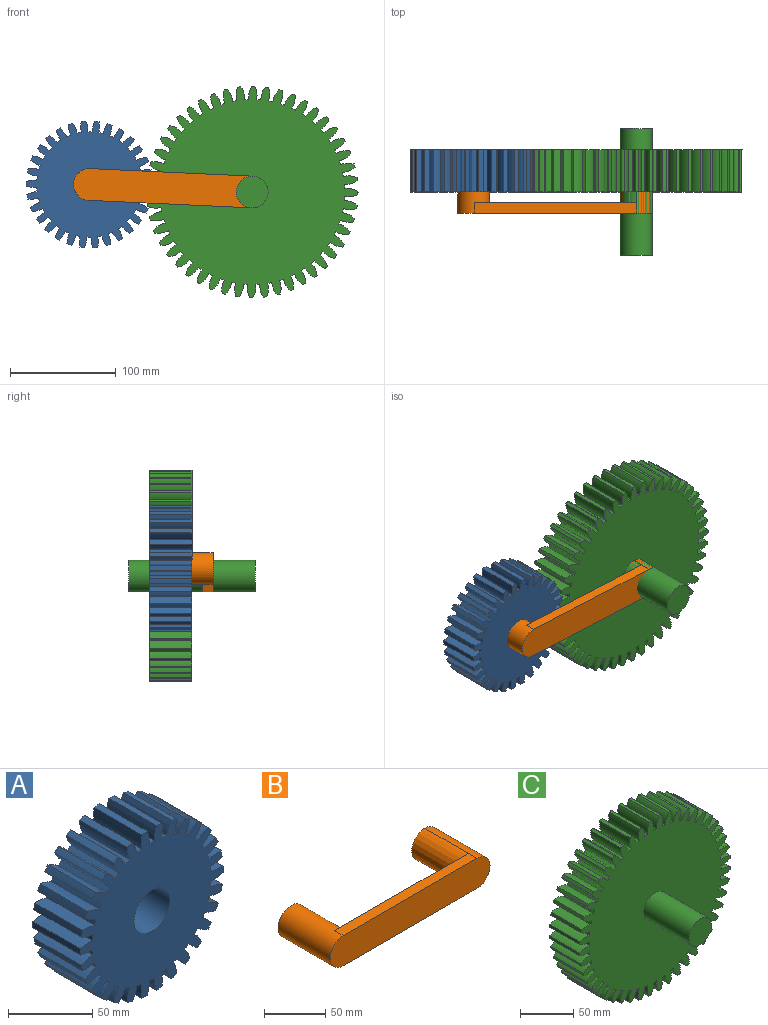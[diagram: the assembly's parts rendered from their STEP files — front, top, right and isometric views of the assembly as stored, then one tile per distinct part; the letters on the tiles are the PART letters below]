
ASSEMBLY  parts=3 mates=2
PART A: 123 faces, bbox 120x40x119.7 mm
  f0: cylinder r=60mm len=40mm, axis (0,1,0), area 182.4mm2, adj f1,f118,f120,f121
  f1: cylinder r=28.31mm len=40mm, axis (0,1,0), area 406.4mm2, adj f0,f3,f120,f121
  f2: cylinder r=28.31mm len=40mm, axis (0,1,0), area 406.4mm2, adj f3,f4,f120,f121
  f3: cylinder r=50mm len=40mm, axis (0,1,0), area 160mm2, adj f1,f2,f120,f121
  f4: cylinder r=60mm len=40mm, axis (0,1,0), area 182.4mm2, adj f2,f5,f120,f121
  f5: cylinder r=28.31mm len=40mm, axis (0,1,0), area 406.4mm2, adj f4,f7,f120,f121
  f6: cylinder r=28.31mm len=40mm, axis (0,1,0), area 406.4mm2, adj f7,f8,f120,f121
  f7: cylinder r=50mm len=40mm, axis (0,1,0), area 160mm2, adj f5,f6,f120,f121
  f8: cylinder r=60mm len=40mm, axis (0,1,0), area 182.4mm2, adj f6,f9,f120,f121
  f9: cylinder r=28.31mm len=40mm, axis (0,1,0), area 406.4mm2, adj f8,f11,f120,f121
  f10: cylinder r=28.31mm len=40mm, axis (0,1,0), area 406.4mm2, adj f11,f12,f120,f121
  f11: cylinder r=50mm len=40mm, axis (0,1,0), area 160mm2, adj f9,f10,f120,f121
  f12: cylinder r=60mm len=40mm, axis (0,1,0), area 182.4mm2, adj f10,f13,f120,f121
  f13: cylinder r=28.31mm len=40mm, axis (0,1,0), area 406.4mm2, adj f12,f15,f120,f121
  f14: cylinder r=28.31mm len=40mm, axis (0,1,0), area 406.4mm2, adj f15,f16,f120,f121
  f15: cylinder r=50mm len=40mm, axis (0,1,0), area 160mm2, adj f13,f14,f120,f121
  f16: cylinder r=60mm len=40mm, axis (0,1,0), area 182.4mm2, adj f14,f17,f120,f121
  f17: cylinder r=28.31mm len=40mm, axis (0,1,0), area 406.4mm2, adj f16,f19,f120,f121
  f18: cylinder r=28.31mm len=40mm, axis (0,1,0), area 406.4mm2, adj f19,f20,f120,f121
  f19: cylinder r=50mm len=40mm, axis (0,1,0), area 160mm2, adj f17,f18,f120,f121
  f20: cylinder r=60mm len=40mm, axis (0,1,0), area 182.4mm2, adj f18,f21,f120,f121
  f21: cylinder r=28.31mm len=40mm, axis (0,1,0), area 406.4mm2, adj f20,f23,f120,f121
  f22: cylinder r=28.31mm len=40mm, axis (0,1,0), area 406.4mm2, adj f23,f24,f120,f121
  f23: cylinder r=50mm len=40mm, axis (0,1,0), area 160mm2, adj f21,f22,f120,f121
  f24: cylinder r=60mm len=40mm, axis (0,1,0), area 182.4mm2, adj f22,f25,f120,f121
  f25: cylinder r=28.31mm len=40mm, axis (0,1,0), area 406.4mm2, adj f24,f27,f120,f121
  f26: cylinder r=28.31mm len=40mm, axis (0,1,0), area 406.4mm2, adj f27,f28,f120,f121
  f27: cylinder r=50mm len=40mm, axis (0,1,0), area 160mm2, adj f25,f26,f120,f121
  f28: cylinder r=60mm len=40mm, axis (0,1,0), area 182.4mm2, adj f26,f29,f120,f121
  f29: cylinder r=28.31mm len=40mm, axis (0,1,0), area 406.4mm2, adj f28,f31,f120,f121
  f30: cylinder r=28.31mm len=40mm, axis (0,1,0), area 406.4mm2, adj f31,f32,f120,f121
  f31: cylinder r=50mm len=40mm, axis (0,1,0), area 160mm2, adj f29,f30,f120,f121
  f32: cylinder r=60mm len=40mm, axis (0,1,0), area 182.4mm2, adj f30,f33,f120,f121
  f33: cylinder r=28.31mm len=40mm, axis (0,1,0), area 406.4mm2, adj f32,f35,f120,f121
  f34: cylinder r=28.31mm len=40mm, axis (0,1,0), area 406.4mm2, adj f35,f36,f120,f121
  f35: cylinder r=50mm len=40mm, axis (0,1,0), area 160mm2, adj f33,f34,f120,f121
  f36: cylinder r=60mm len=40mm, axis (0,1,0), area 182.4mm2, adj f34,f37,f120,f121
  f37: cylinder r=28.31mm len=40mm, axis (0,1,0), area 406.4mm2, adj f36,f39,f120,f121
  f38: cylinder r=28.31mm len=40mm, axis (0,1,0), area 406.4mm2, adj f39,f40,f120,f121
  f39: cylinder r=50mm len=40mm, axis (0,1,0), area 160mm2, adj f37,f38,f120,f121
  f40: cylinder r=60mm len=40mm, axis (0,1,0), area 182.4mm2, adj f38,f41,f120,f121
  f41: cylinder r=28.31mm len=40mm, axis (0,1,0), area 406.4mm2, adj f40,f43,f120,f121
  f42: cylinder r=28.31mm len=40mm, axis (0,1,0), area 406.4mm2, adj f43,f44,f120,f121
  f43: cylinder r=50mm len=40mm, axis (0,1,0), area 160mm2, adj f41,f42,f120,f121
  f44: cylinder r=60mm len=40mm, axis (0,1,0), area 182.4mm2, adj f42,f45,f120,f121
  f45: cylinder r=28.31mm len=40mm, axis (0,1,0), area 406.4mm2, adj f44,f47,f120,f121
  f46: cylinder r=28.31mm len=40mm, axis (0,1,0), area 406.4mm2, adj f47,f48,f120,f121
  f47: cylinder r=50mm len=40mm, axis (0,1,0), area 160mm2, adj f45,f46,f120,f121
  f48: cylinder r=60mm len=40mm, axis (0,1,0), area 182.4mm2, adj f46,f49,f120,f121
  f49: cylinder r=28.31mm len=40mm, axis (0,1,0), area 406.4mm2, adj f48,f51,f120,f121
  f50: cylinder r=28.31mm len=40mm, axis (0,1,0), area 406.4mm2, adj f51,f52,f120,f121
  f51: cylinder r=50mm len=40mm, axis (0,1,0), area 160mm2, adj f49,f50,f120,f121
  f52: cylinder r=60mm len=40mm, axis (0,1,0), area 182.4mm2, adj f50,f53,f120,f121
  f53: cylinder r=28.31mm len=40mm, axis (0,1,0), area 406.4mm2, adj f52,f55,f120,f121
  f54: cylinder r=28.31mm len=40mm, axis (0,1,0), area 406.4mm2, adj f55,f56,f120,f121
  f55: cylinder r=50mm len=40mm, axis (0,1,0), area 160mm2, adj f53,f54,f120,f121
  f56: cylinder r=60mm len=40mm, axis (0,1,0), area 182.4mm2, adj f54,f57,f120,f121
  f57: cylinder r=28.31mm len=40mm, axis (0,1,0), area 406.4mm2, adj f56,f59,f120,f121
  f58: cylinder r=28.31mm len=40mm, axis (0,1,0), area 406.4mm2, adj f59,f60,f120,f121
  f59: cylinder r=50mm len=40mm, axis (0,1,0), area 160mm2, adj f57,f58,f120,f121
  f60: cylinder r=60mm len=40mm, axis (0,1,0), area 182.4mm2, adj f58,f61,f120,f121
  f61: cylinder r=28.31mm len=40mm, axis (0,1,0), area 406.4mm2, adj f60,f63,f120,f121
  f62: cylinder r=28.31mm len=40mm, axis (0,1,0), area 406.4mm2, adj f63,f64,f120,f121
  f63: cylinder r=50mm len=40mm, axis (0,1,0), area 160mm2, adj f61,f62,f120,f121
  f64: cylinder r=60mm len=40mm, axis (0,1,0), area 182.4mm2, adj f62,f65,f120,f121
  f65: cylinder r=28.31mm len=40mm, axis (0,1,0), area 406.4mm2, adj f64,f67,f120,f121
  f66: cylinder r=28.31mm len=40mm, axis (0,1,0), area 406.4mm2, adj f67,f68,f120,f121
  f67: cylinder r=50mm len=40mm, axis (0,1,0), area 160mm2, adj f65,f66,f120,f121
  f68: cylinder r=60mm len=40mm, axis (0,1,0), area 182.4mm2, adj f66,f69,f120,f121
  f69: cylinder r=28.31mm len=40mm, axis (0,1,0), area 406.4mm2, adj f68,f71,f120,f121
  f70: cylinder r=28.31mm len=40mm, axis (0,1,0), area 406.4mm2, adj f71,f72,f120,f121
  f71: cylinder r=50mm len=40mm, axis (0,1,0), area 160mm2, adj f69,f70,f120,f121
  f72: cylinder r=60mm len=40mm, axis (0,1,0), area 182.4mm2, adj f70,f73,f120,f121
  f73: cylinder r=28.31mm len=40mm, axis (0,1,0), area 406.4mm2, adj f72,f75,f120,f121
  f74: cylinder r=28.31mm len=40mm, axis (0,1,0), area 406.4mm2, adj f75,f76,f120,f121
  f75: cylinder r=50mm len=40mm, axis (0,1,0), area 160mm2, adj f73,f74,f120,f121
  f76: cylinder r=60mm len=40mm, axis (0,1,0), area 182.4mm2, adj f74,f77,f120,f121
  f77: cylinder r=28.31mm len=40mm, axis (0,1,0), area 406.4mm2, adj f76,f79,f120,f121
  f78: cylinder r=28.31mm len=40mm, axis (0,1,0), area 406.4mm2, adj f79,f80,f120,f121
  f79: cylinder r=50mm len=40mm, axis (0,1,0), area 160mm2, adj f77,f78,f120,f121
  f80: cylinder r=60mm len=40mm, axis (0,1,0), area 182.4mm2, adj f78,f81,f120,f121
  f81: cylinder r=28.31mm len=40mm, axis (0,1,0), area 406.4mm2, adj f80,f83,f120,f121
  f82: cylinder r=28.31mm len=40mm, axis (0,1,0), area 406.4mm2, adj f83,f84,f120,f121
  f83: cylinder r=50mm len=40mm, axis (0,1,0), area 160mm2, adj f81,f82,f120,f121
  f84: cylinder r=60mm len=40mm, axis (0,1,0), area 182.4mm2, adj f82,f85,f120,f121
  f85: cylinder r=28.31mm len=40mm, axis (0,1,0), area 406.4mm2, adj f84,f87,f120,f121
  f86: cylinder r=28.31mm len=40mm, axis (0,1,0), area 406.4mm2, adj f87,f88,f120,f121
  f87: cylinder r=50mm len=40mm, axis (0,1,0), area 160mm2, adj f85,f86,f120,f121
  f88: cylinder r=60mm len=40mm, axis (0,1,0), area 182.4mm2, adj f86,f89,f120,f121
  f89: cylinder r=28.31mm len=40mm, axis (0,1,0), area 406.4mm2, adj f88,f91,f120,f121
  f90: cylinder r=28.31mm len=40mm, axis (0,1,0), area 406.4mm2, adj f91,f92,f120,f121
  f91: cylinder r=50mm len=40mm, axis (0,1,0), area 160mm2, adj f89,f90,f120,f121
  f92: cylinder r=60mm len=40mm, axis (0,1,0), area 182.4mm2, adj f90,f93,f120,f121
  f93: cylinder r=28.31mm len=40mm, axis (0,1,0), area 406.4mm2, adj f92,f95,f120,f121
  f94: cylinder r=28.31mm len=40mm, axis (0,1,0), area 406.4mm2, adj f95,f96,f120,f121
  f95: cylinder r=50mm len=40mm, axis (0,1,0), area 160mm2, adj f93,f94,f120,f121
  f96: cylinder r=60mm len=40mm, axis (0,1,0), area 182.4mm2, adj f94,f97,f120,f121
  f97: cylinder r=28.31mm len=40mm, axis (0,1,0), area 406.4mm2, adj f96,f99,f120,f121
  f98: cylinder r=28.31mm len=40mm, axis (0,1,0), area 406.4mm2, adj f99,f100,f120,f121
  f99: cylinder r=50mm len=40mm, axis (0,1,0), area 160mm2, adj f97,f98,f120,f121
  f100: cylinder r=60mm len=40mm, axis (0,1,0), area 182.4mm2, adj f98,f101,f120,f121
  f101: cylinder r=28.31mm len=40mm, axis (0,1,0), area 406.4mm2, adj f100,f103,f120,f121
  f102: cylinder r=28.31mm len=40mm, axis (0,1,0), area 406.4mm2, adj f103,f104,f120,f121
  f103: cylinder r=50mm len=40mm, axis (0,1,0), area 160mm2, adj f101,f102,f120,f121
  f104: cylinder r=60mm len=40mm, axis (0,1,0), area 182.4mm2, adj f102,f105,f120,f121
  f105: cylinder r=28.31mm len=40mm, axis (0,1,0), area 406.4mm2, adj f104,f107,f120,f121
  f106: cylinder r=28.31mm len=40mm, axis (0,1,0), area 406.4mm2, adj f107,f108,f120,f121
  f107: cylinder r=50mm len=40mm, axis (0,1,0), area 160mm2, adj f105,f106,f120,f121
  f108: cylinder r=60mm len=40mm, axis (0,1,0), area 182.4mm2, adj f106,f109,f120,f121
  f109: cylinder r=28.31mm len=40mm, axis (0,1,0), area 406.4mm2, adj f108,f111,f120,f121
  f110: cylinder r=28.31mm len=40mm, axis (0,1,0), area 406.4mm2, adj f111,f112,f120,f121
  f111: cylinder r=50mm len=40mm, axis (0,1,0), area 160mm2, adj f109,f110,f120,f121
  f112: cylinder r=60mm len=40mm, axis (0,1,0), area 182.4mm2, adj f110,f113,f120,f121
  f113: cylinder r=28.31mm len=40mm, axis (0,1,0), area 406.4mm2, adj f112,f115,f120,f121
  f114: cylinder r=28.31mm len=40mm, axis (0,1,0), area 406.4mm2, adj f115,f117,f120,f121
  f115: cylinder r=50mm len=40mm, axis (0,1,0), area 160mm2, adj f113,f114,f120,f121
  f116: cylinder r=28.31mm len=40mm, axis (0,1,0), area 406.4mm2, adj f117,f119,f120,f121
  f117: cylinder r=60mm len=40mm, axis (0,1,0), area 182.4mm2, adj f114,f116,f120,f121
  f118: cylinder r=28.31mm len=40mm, axis (0,1,0), area 406.4mm2, adj f0,f119,f120,f121
  f119: cylinder r=50mm len=40mm, axis (0,1,0), area 160mm2, adj f116,f118,f120,f121
  f120: plane 120x119.73mm, normal (0,-1,0), area 8985.6mm2, adj f0,f1,f2,f3,f4,f5,f6,f7
  f121: plane 120x119.73mm, normal (0,1,0), area 8985.6mm2, adj f0,f1,f2,f3,f4,f5,f6,f7
  f122: cylinder r=15mm len=40mm, axis (0,-1,0), area 3769.9mm2, adj f120,f121
PART B: 9 faces, bbox 184x60x30 mm
  f0: cylinder r=15mm len=60mm, axis (0,1,0), area 5183.6mm2, adj f1,f2,f3,f4,f5
  f1: plane 184x30mm, normal (0,-1,0), area 5326.9mm2, adj f0,f4,f5,f6
  f2: plane 30x30mm, normal (0,1,0), area 706.9mm2, adj f0
  f3: plane 154x30mm, normal (0,1,0), area 3913.2mm2, adj f0,f4,f5,f7
  f4: plane 154x10mm, normal (0,0,1), area 1540mm2, adj f0,f1,f3,f6
  f5: plane 154x10mm, normal (0,0,-1), area 1540mm2, adj f0,f1,f3,f6
  f6: cylinder r=15mm len=60mm, axis (0,-1,0), area 2827.4mm2, adj f1,f4,f5,f7,f8
  f7: extruded ~50x30mm, area 2356.6mm2, adj f3,f6,f8
  f8: plane 30x30mm, normal (0,1,0), area 706.8mm2, adj f6,f7
PART C: 198 faces, bbox 199.8x120x199.8 mm
  f0: cylinder r=100mm len=40mm, axis (0,1,0), area 123.4mm2, adj f1,f188,f192,f193
  f1: cylinder r=19.38mm len=40mm, axis (0,1,0), area 517.2mm2, adj f0,f3,f192,f193
  f2: cylinder r=19.56mm len=40mm, axis (0,1,0), area 522.9mm2, adj f3,f4,f192,f193
  f3: cylinder r=87.5mm len=40mm, axis (0,1,0), area 160mm2, adj f1,f2,f192,f193
  f4: cylinder r=100mm len=40mm, axis (0,1,0), area 123.4mm2, adj f2,f5,f192,f193
  f5: cylinder r=19.38mm len=40mm, axis (0,1,0), area 517.2mm2, adj f4,f7,f192,f193
  f6: cylinder r=19.56mm len=40mm, axis (0,1,0), area 522.9mm2, adj f7,f8,f192,f193
  f7: cylinder r=87.5mm len=40mm, axis (0,1,0), area 160mm2, adj f5,f6,f192,f193
  f8: cylinder r=100mm len=40mm, axis (0,1,0), area 123.4mm2, adj f6,f9,f192,f193
  f9: cylinder r=19.38mm len=40mm, axis (0,1,0), area 517.2mm2, adj f8,f11,f192,f193
  f10: cylinder r=19.56mm len=40mm, axis (0,1,0), area 522.9mm2, adj f11,f12,f192,f193
  f11: cylinder r=87.5mm len=40mm, axis (0,1,0), area 160mm2, adj f9,f10,f192,f193
  f12: cylinder r=100mm len=40mm, axis (0,1,0), area 123.4mm2, adj f10,f13,f192,f193
  f13: cylinder r=19.38mm len=40mm, axis (0,1,0), area 517.2mm2, adj f12,f15,f192,f193
  f14: cylinder r=19.56mm len=40mm, axis (0,1,0), area 522.9mm2, adj f15,f16,f192,f193
  f15: cylinder r=87.5mm len=40mm, axis (0,1,0), area 160mm2, adj f13,f14,f192,f193
  f16: cylinder r=100mm len=40mm, axis (0,1,0), area 123.4mm2, adj f14,f17,f192,f193
  f17: cylinder r=19.38mm len=40mm, axis (0,1,0), area 517.2mm2, adj f16,f19,f192,f193
  f18: cylinder r=19.56mm len=40mm, axis (0,1,0), area 522.9mm2, adj f19,f20,f192,f193
  f19: cylinder r=87.5mm len=40mm, axis (0,1,0), area 160mm2, adj f17,f18,f192,f193
  f20: cylinder r=100mm len=40mm, axis (0,1,0), area 123.4mm2, adj f18,f21,f192,f193
  f21: cylinder r=19.38mm len=40mm, axis (0,1,0), area 517.2mm2, adj f20,f23,f192,f193
  f22: cylinder r=19.56mm len=40mm, axis (0,1,0), area 522.9mm2, adj f23,f24,f192,f193
  f23: cylinder r=87.5mm len=40mm, axis (0,1,0), area 160mm2, adj f21,f22,f192,f193
  f24: cylinder r=100mm len=40mm, axis (0,1,0), area 123.4mm2, adj f22,f25,f192,f193
  f25: cylinder r=19.38mm len=40mm, axis (0,1,0), area 517.2mm2, adj f24,f27,f192,f193
  f26: cylinder r=19.56mm len=40mm, axis (0,1,0), area 522.9mm2, adj f27,f28,f192,f193
  f27: cylinder r=87.5mm len=40mm, axis (0,1,0), area 160mm2, adj f25,f26,f192,f193
  f28: cylinder r=100mm len=40mm, axis (0,1,0), area 123.4mm2, adj f26,f29,f192,f193
  f29: cylinder r=19.38mm len=40mm, axis (0,1,0), area 517.2mm2, adj f28,f31,f192,f193
  f30: cylinder r=19.56mm len=40mm, axis (0,1,0), area 522.9mm2, adj f31,f32,f192,f193
  f31: cylinder r=87.5mm len=40mm, axis (0,1,0), area 160mm2, adj f29,f30,f192,f193
  f32: cylinder r=100mm len=40mm, axis (0,1,0), area 123.4mm2, adj f30,f33,f192,f193
  f33: cylinder r=19.38mm len=40mm, axis (0,1,0), area 517.2mm2, adj f32,f35,f192,f193
  f34: cylinder r=19.56mm len=40mm, axis (0,1,0), area 522.9mm2, adj f35,f36,f192,f193
  f35: cylinder r=87.5mm len=40mm, axis (0,1,0), area 160mm2, adj f33,f34,f192,f193
  f36: cylinder r=100mm len=40mm, axis (0,1,0), area 123.4mm2, adj f34,f37,f192,f193
  f37: cylinder r=19.38mm len=40mm, axis (0,1,0), area 517.2mm2, adj f36,f39,f192,f193
  f38: cylinder r=19.56mm len=40mm, axis (0,1,0), area 522.9mm2, adj f39,f40,f192,f193
  f39: cylinder r=87.5mm len=40mm, axis (0,1,0), area 160mm2, adj f37,f38,f192,f193
  f40: cylinder r=100mm len=40mm, axis (0,1,0), area 123.4mm2, adj f38,f41,f192,f193
  f41: cylinder r=19.38mm len=40mm, axis (0,1,0), area 517.2mm2, adj f40,f43,f192,f193
  f42: cylinder r=19.56mm len=40mm, axis (0,1,0), area 522.9mm2, adj f43,f44,f192,f193
  f43: cylinder r=87.5mm len=40mm, axis (0,1,0), area 160mm2, adj f41,f42,f192,f193
  f44: cylinder r=100mm len=40mm, axis (0,1,0), area 123.4mm2, adj f42,f45,f192,f193
  f45: cylinder r=19.38mm len=40mm, axis (0,1,0), area 517.2mm2, adj f44,f47,f192,f193
  f46: cylinder r=19.56mm len=40mm, axis (0,1,0), area 522.9mm2, adj f47,f48,f192,f193
  f47: cylinder r=87.5mm len=40mm, axis (0,1,0), area 160mm2, adj f45,f46,f192,f193
  f48: cylinder r=100mm len=40mm, axis (0,1,0), area 123.4mm2, adj f46,f49,f192,f193
  f49: cylinder r=19.38mm len=40mm, axis (0,1,0), area 517.2mm2, adj f48,f51,f192,f193
  f50: cylinder r=19.56mm len=40mm, axis (0,1,0), area 522.9mm2, adj f51,f52,f192,f193
  f51: cylinder r=87.5mm len=40mm, axis (0,1,0), area 160mm2, adj f49,f50,f192,f193
  f52: cylinder r=100mm len=40mm, axis (0,1,0), area 123.4mm2, adj f50,f53,f192,f193
  f53: cylinder r=19.38mm len=40mm, axis (0,1,0), area 517.2mm2, adj f52,f55,f192,f193
  f54: cylinder r=19.56mm len=40mm, axis (0,1,0), area 522.9mm2, adj f55,f56,f192,f193
  f55: cylinder r=87.5mm len=40mm, axis (0,1,0), area 160mm2, adj f53,f54,f192,f193
  f56: cylinder r=100mm len=40mm, axis (0,1,0), area 123.4mm2, adj f54,f57,f192,f193
  f57: cylinder r=19.38mm len=40mm, axis (0,1,0), area 517.2mm2, adj f56,f59,f192,f193
  f58: cylinder r=19.56mm len=40mm, axis (0,1,0), area 522.9mm2, adj f59,f60,f192,f193
  f59: cylinder r=87.5mm len=40mm, axis (0,1,0), area 160mm2, adj f57,f58,f192,f193
  f60: cylinder r=100mm len=40mm, axis (0,1,0), area 123.4mm2, adj f58,f61,f192,f193
  f61: cylinder r=19.38mm len=40mm, axis (0,1,0), area 517.2mm2, adj f60,f63,f192,f193
  f62: cylinder r=19.56mm len=40mm, axis (0,1,0), area 522.9mm2, adj f63,f64,f192,f193
  f63: cylinder r=87.5mm len=40mm, axis (0,1,0), area 160mm2, adj f61,f62,f192,f193
  f64: cylinder r=100mm len=40mm, axis (0,1,0), area 123.4mm2, adj f62,f65,f192,f193
  f65: cylinder r=19.38mm len=40mm, axis (0,1,0), area 517.2mm2, adj f64,f67,f192,f193
  f66: cylinder r=19.56mm len=40mm, axis (0,1,0), area 522.9mm2, adj f67,f68,f192,f193
  f67: cylinder r=87.5mm len=40mm, axis (0,1,0), area 160mm2, adj f65,f66,f192,f193
  f68: cylinder r=100mm len=40mm, axis (0,1,0), area 123.4mm2, adj f66,f69,f192,f193
  f69: cylinder r=19.38mm len=40mm, axis (0,1,0), area 517.2mm2, adj f68,f71,f192,f193
  f70: cylinder r=19.56mm len=40mm, axis (0,1,0), area 522.9mm2, adj f71,f72,f192,f193
  f71: cylinder r=87.5mm len=40mm, axis (0,1,0), area 160mm2, adj f69,f70,f192,f193
  f72: cylinder r=100mm len=40mm, axis (0,1,0), area 123.4mm2, adj f70,f73,f192,f193
  f73: cylinder r=19.38mm len=40mm, axis (0,1,0), area 517.2mm2, adj f72,f75,f192,f193
  f74: cylinder r=19.56mm len=40mm, axis (0,1,0), area 522.9mm2, adj f75,f76,f192,f193
  f75: cylinder r=87.5mm len=40mm, axis (0,1,0), area 160mm2, adj f73,f74,f192,f193
  f76: cylinder r=100mm len=40mm, axis (0,1,0), area 123.4mm2, adj f74,f77,f192,f193
  f77: cylinder r=19.38mm len=40mm, axis (0,1,0), area 517.2mm2, adj f76,f79,f192,f193
  f78: cylinder r=19.56mm len=40mm, axis (0,1,0), area 522.9mm2, adj f79,f80,f192,f193
  f79: cylinder r=87.5mm len=40mm, axis (0,1,0), area 160mm2, adj f77,f78,f192,f193
  f80: cylinder r=100mm len=40mm, axis (0,1,0), area 123.4mm2, adj f78,f81,f192,f193
  f81: cylinder r=19.38mm len=40mm, axis (0,1,0), area 517.2mm2, adj f80,f83,f192,f193
  f82: cylinder r=19.56mm len=40mm, axis (0,1,0), area 522.9mm2, adj f83,f84,f192,f193
  f83: cylinder r=87.5mm len=40mm, axis (0,1,0), area 160mm2, adj f81,f82,f192,f193
  f84: cylinder r=100mm len=40mm, axis (0,1,0), area 123.4mm2, adj f82,f85,f192,f193
  f85: cylinder r=19.38mm len=40mm, axis (0,1,0), area 517.2mm2, adj f84,f87,f192,f193
  f86: cylinder r=19.56mm len=40mm, axis (0,1,0), area 522.9mm2, adj f87,f88,f192,f193
  f87: cylinder r=87.5mm len=40mm, axis (0,1,0), area 160mm2, adj f85,f86,f192,f193
  f88: cylinder r=100mm len=40mm, axis (0,1,0), area 123.4mm2, adj f86,f89,f192,f193
  f89: cylinder r=19.38mm len=40mm, axis (0,1,0), area 517.2mm2, adj f88,f91,f192,f193
  f90: cylinder r=19.56mm len=40mm, axis (0,1,0), area 522.9mm2, adj f91,f92,f192,f193
  f91: cylinder r=87.5mm len=40mm, axis (0,1,0), area 160mm2, adj f89,f90,f192,f193
  f92: cylinder r=100mm len=40mm, axis (0,1,0), area 123.4mm2, adj f90,f93,f192,f193
  f93: cylinder r=19.38mm len=40mm, axis (0,1,0), area 517.2mm2, adj f92,f95,f192,f193
  f94: cylinder r=19.56mm len=40mm, axis (0,1,0), area 522.9mm2, adj f95,f96,f192,f193
  f95: cylinder r=87.5mm len=40mm, axis (0,1,0), area 160mm2, adj f93,f94,f192,f193
  f96: cylinder r=100mm len=40mm, axis (0,1,0), area 123.4mm2, adj f94,f97,f192,f193
  f97: cylinder r=19.38mm len=40mm, axis (0,1,0), area 517.2mm2, adj f96,f99,f192,f193
  f98: cylinder r=19.56mm len=40mm, axis (0,1,0), area 522.9mm2, adj f99,f100,f192,f193
  f99: cylinder r=87.5mm len=40mm, axis (0,1,0), area 160mm2, adj f97,f98,f192,f193
  f100: cylinder r=100mm len=40mm, axis (0,1,0), area 123.4mm2, adj f98,f101,f192,f193
  f101: cylinder r=19.38mm len=40mm, axis (0,1,0), area 517.2mm2, adj f100,f103,f192,f193
  f102: cylinder r=19.56mm len=40mm, axis (0,1,0), area 522.9mm2, adj f103,f104,f192,f193
  f103: cylinder r=87.5mm len=40mm, axis (0,1,0), area 160mm2, adj f101,f102,f192,f193
  f104: cylinder r=100mm len=40mm, axis (0,1,0), area 123.4mm2, adj f102,f105,f192,f193
  f105: cylinder r=19.38mm len=40mm, axis (0,1,0), area 517.2mm2, adj f104,f107,f192,f193
  f106: cylinder r=19.56mm len=40mm, axis (0,1,0), area 522.9mm2, adj f107,f108,f192,f193
  f107: cylinder r=87.5mm len=40mm, axis (0,1,0), area 160mm2, adj f105,f106,f192,f193
  f108: cylinder r=100mm len=40mm, axis (0,1,0), area 123.4mm2, adj f106,f109,f192,f193
  f109: cylinder r=19.38mm len=40mm, axis (0,1,0), area 517.2mm2, adj f108,f111,f192,f193
  f110: cylinder r=19.56mm len=40mm, axis (0,1,0), area 522.9mm2, adj f111,f112,f192,f193
  f111: cylinder r=87.5mm len=40mm, axis (0,1,0), area 160mm2, adj f109,f110,f192,f193
  f112: cylinder r=100mm len=40mm, axis (0,1,0), area 123.4mm2, adj f110,f113,f192,f193
  f113: cylinder r=19.38mm len=40mm, axis (0,1,0), area 517.2mm2, adj f112,f115,f192,f193
  f114: cylinder r=19.56mm len=40mm, axis (0,1,0), area 522.9mm2, adj f115,f116,f192,f193
  f115: cylinder r=87.5mm len=40mm, axis (0,1,0), area 160mm2, adj f113,f114,f192,f193
  f116: cylinder r=100mm len=40mm, axis (0,1,0), area 123.4mm2, adj f114,f117,f192,f193
  f117: cylinder r=19.38mm len=40mm, axis (0,1,0), area 517.2mm2, adj f116,f119,f192,f193
  f118: cylinder r=19.56mm len=40mm, axis (0,1,0), area 522.9mm2, adj f119,f120,f192,f193
  f119: cylinder r=87.5mm len=40mm, axis (0,1,0), area 160mm2, adj f117,f118,f192,f193
  f120: cylinder r=100mm len=40mm, axis (0,1,0), area 123.4mm2, adj f118,f121,f192,f193
  f121: cylinder r=19.38mm len=40mm, axis (0,1,0), area 517.2mm2, adj f120,f123,f192,f193
  f122: cylinder r=19.56mm len=40mm, axis (0,1,0), area 522.9mm2, adj f123,f124,f192,f193
  f123: cylinder r=87.5mm len=40mm, axis (0,1,0), area 160mm2, adj f121,f122,f192,f193
  f124: cylinder r=100mm len=40mm, axis (0,1,0), area 123.4mm2, adj f122,f125,f192,f193
  f125: cylinder r=19.38mm len=40mm, axis (0,1,0), area 517.2mm2, adj f124,f127,f192,f193
  f126: cylinder r=19.56mm len=40mm, axis (0,1,0), area 522.9mm2, adj f127,f128,f192,f193
  f127: cylinder r=87.5mm len=40mm, axis (0,1,0), area 160mm2, adj f125,f126,f192,f193
  f128: cylinder r=100mm len=40mm, axis (0,1,0), area 123.4mm2, adj f126,f129,f192,f193
  f129: cylinder r=19.38mm len=40mm, axis (0,1,0), area 517.2mm2, adj f128,f131,f192,f193
  f130: cylinder r=19.56mm len=40mm, axis (0,1,0), area 522.9mm2, adj f131,f132,f192,f193
  f131: cylinder r=87.5mm len=40mm, axis (0,1,0), area 160mm2, adj f129,f130,f192,f193
  f132: cylinder r=100mm len=40mm, axis (0,1,0), area 123.4mm2, adj f130,f133,f192,f193
  f133: cylinder r=19.38mm len=40mm, axis (0,1,0), area 517.2mm2, adj f132,f135,f192,f193
  f134: cylinder r=19.56mm len=40mm, axis (0,1,0), area 522.9mm2, adj f135,f136,f192,f193
  f135: cylinder r=87.5mm len=40mm, axis (0,1,0), area 160mm2, adj f133,f134,f192,f193
  f136: cylinder r=100mm len=40mm, axis (0,1,0), area 123.4mm2, adj f134,f137,f192,f193
  f137: cylinder r=19.38mm len=40mm, axis (0,1,0), area 517.2mm2, adj f136,f139,f192,f193
  f138: cylinder r=19.56mm len=40mm, axis (0,1,0), area 522.9mm2, adj f139,f140,f192,f193
  f139: cylinder r=87.5mm len=40mm, axis (0,1,0), area 160mm2, adj f137,f138,f192,f193
  f140: cylinder r=100mm len=40mm, axis (0,1,0), area 123.4mm2, adj f138,f141,f192,f193
  f141: cylinder r=19.38mm len=40mm, axis (0,1,0), area 517.2mm2, adj f140,f143,f192,f193
  f142: cylinder r=19.56mm len=40mm, axis (0,1,0), area 522.9mm2, adj f143,f144,f192,f193
  f143: cylinder r=87.5mm len=40mm, axis (0,1,0), area 160mm2, adj f141,f142,f192,f193
  f144: cylinder r=100mm len=40mm, axis (0,1,0), area 123.4mm2, adj f142,f145,f192,f193
  f145: cylinder r=19.38mm len=40mm, axis (0,1,0), area 517.2mm2, adj f144,f147,f192,f193
  f146: cylinder r=19.56mm len=40mm, axis (0,1,0), area 522.9mm2, adj f147,f148,f192,f193
  f147: cylinder r=87.5mm len=40mm, axis (0,1,0), area 160mm2, adj f145,f146,f192,f193
  f148: cylinder r=100mm len=40mm, axis (0,1,0), area 123.4mm2, adj f146,f149,f192,f193
  f149: cylinder r=19.38mm len=40mm, axis (0,1,0), area 517.2mm2, adj f148,f151,f192,f193
  f150: cylinder r=19.56mm len=40mm, axis (0,1,0), area 522.9mm2, adj f151,f152,f192,f193
  f151: cylinder r=87.5mm len=40mm, axis (0,1,0), area 160mm2, adj f149,f150,f192,f193
  f152: cylinder r=100mm len=40mm, axis (0,1,0), area 123.4mm2, adj f150,f153,f192,f193
  f153: cylinder r=19.38mm len=40mm, axis (0,1,0), area 517.2mm2, adj f152,f155,f192,f193
  f154: cylinder r=19.56mm len=40mm, axis (0,1,0), area 522.9mm2, adj f155,f156,f192,f193
  f155: cylinder r=87.5mm len=40mm, axis (0,1,0), area 160mm2, adj f153,f154,f192,f193
  f156: cylinder r=100mm len=40mm, axis (0,1,0), area 123.4mm2, adj f154,f157,f192,f193
  f157: cylinder r=19.38mm len=40mm, axis (0,1,0), area 517.2mm2, adj f156,f159,f192,f193
  f158: cylinder r=19.56mm len=40mm, axis (0,1,0), area 522.9mm2, adj f159,f160,f192,f193
  f159: cylinder r=87.5mm len=40mm, axis (0,1,0), area 160mm2, adj f157,f158,f192,f193
  f160: cylinder r=100mm len=40mm, axis (0,1,0), area 123.4mm2, adj f158,f161,f192,f193
  f161: cylinder r=19.38mm len=40mm, axis (0,1,0), area 517.2mm2, adj f160,f163,f192,f193
  f162: cylinder r=19.56mm len=40mm, axis (0,1,0), area 522.9mm2, adj f163,f164,f192,f193
  f163: cylinder r=87.5mm len=40mm, axis (0,1,0), area 160mm2, adj f161,f162,f192,f193
  f164: cylinder r=100mm len=40mm, axis (0,1,0), area 123.4mm2, adj f162,f165,f192,f193
  f165: cylinder r=19.38mm len=40mm, axis (0,1,0), area 517.2mm2, adj f164,f167,f192,f193
  f166: cylinder r=19.56mm len=40mm, axis (0,1,0), area 522.9mm2, adj f167,f168,f192,f193
  f167: cylinder r=87.5mm len=40mm, axis (0,1,0), area 160mm2, adj f165,f166,f192,f193
  f168: cylinder r=100mm len=40mm, axis (0,1,0), area 123.4mm2, adj f166,f169,f192,f193
  f169: cylinder r=19.38mm len=40mm, axis (0,1,0), area 517.2mm2, adj f168,f171,f192,f193
  f170: cylinder r=19.56mm len=40mm, axis (0,1,0), area 522.9mm2, adj f171,f172,f192,f193
  f171: cylinder r=87.5mm len=40mm, axis (0,1,0), area 160mm2, adj f169,f170,f192,f193
  f172: cylinder r=100mm len=40mm, axis (0,1,0), area 123.4mm2, adj f170,f173,f192,f193
  f173: cylinder r=19.38mm len=40mm, axis (0,1,0), area 517.2mm2, adj f172,f175,f192,f193
  f174: cylinder r=19.56mm len=40mm, axis (0,1,0), area 522.9mm2, adj f175,f176,f192,f193
  f175: cylinder r=87.5mm len=40mm, axis (0,1,0), area 160mm2, adj f173,f174,f192,f193
  f176: cylinder r=100mm len=40mm, axis (0,1,0), area 123.4mm2, adj f174,f177,f192,f193
  f177: cylinder r=19.38mm len=40mm, axis (0,1,0), area 517.2mm2, adj f176,f179,f192,f193
  f178: cylinder r=19.56mm len=40mm, axis (0,1,0), area 522.9mm2, adj f179,f180,f192,f193
  f179: cylinder r=87.5mm len=40mm, axis (0,1,0), area 160mm2, adj f177,f178,f192,f193
  f180: cylinder r=100mm len=40mm, axis (0,1,0), area 123.4mm2, adj f178,f181,f192,f193
  f181: cylinder r=19.38mm len=40mm, axis (0,1,0), area 517.2mm2, adj f180,f183,f192,f193
  f182: cylinder r=19.56mm len=40mm, axis (0,1,0), area 522.9mm2, adj f183,f184,f192,f193
  f183: cylinder r=87.5mm len=40mm, axis (0,1,0), area 160mm2, adj f181,f182,f192,f193
  f184: cylinder r=100mm len=40mm, axis (0,1,0), area 123.4mm2, adj f182,f185,f192,f193
  f185: cylinder r=19.38mm len=40mm, axis (0,1,0), area 517.2mm2, adj f184,f187,f192,f193
  f186: cylinder r=19.56mm len=40mm, axis (0,1,0), area 522.9mm2, adj f187,f191,f192,f193
  f187: cylinder r=87.5mm len=40mm, axis (0,1,0), area 160mm2, adj f185,f186,f192,f193
  f188: cylinder r=19.56mm len=40mm, axis (0,1,0), area 522.9mm2, adj f0,f189,f192,f193
  f189: cylinder r=87.5mm len=40mm, axis (0,1,0), area 160mm2, adj f188,f190,f192,f193
  f190: cylinder r=19.38mm len=40mm, axis (0,1,0), area 517.2mm2, adj f189,f191,f192,f193
  f191: cylinder r=100mm len=40mm, axis (0,1,0), area 123.4mm2, adj f186,f190,f192,f193
  f192: plane 199.79x199.79mm, normal (0,-1,0), area 27389.1mm2, adj f0,f1,f2,f3,f4,f5,f6,f7
  f193: plane 199.79x199.79mm, normal (0,1,0), area 27389.1mm2, adj f0,f1,f2,f3,f4,f5,f6,f7
  f194: plane 30x30mm, normal (0,1,0), area 706.9mm2, adj f195
  f195: cylinder r=15mm len=30mm, axis (0,1,0), area 1885mm2, adj f193,f194
  f196: cylinder r=15mm len=60mm, axis (0,1,0), area 5654.9mm2, adj f192,f197
  f197: plane 30x30mm, normal (0,-1,0), area 706.9mm2, adj f196
PLACE A rot(axis=(0,-1,0),11.3deg) t=(-18.92,-296.89,-14.41)mm
PLACE B rot(axis=(0,1,0),2.7deg) t=(-18.92,-296.89,-14.41)mm fixed
PLACE C rot(axis=(0,1,0),4.1deg) t=(134.92,-296.89,-21.54)mm
MATE revolute B.f6 <-> C.f195  axis (0,1,0) through (134.92,-296.89,-21.54)mm
MATE revolute A.f122 <-> B.f0  axis (0,-1,0) through (-18.92,-336.89,-14.41)mm
